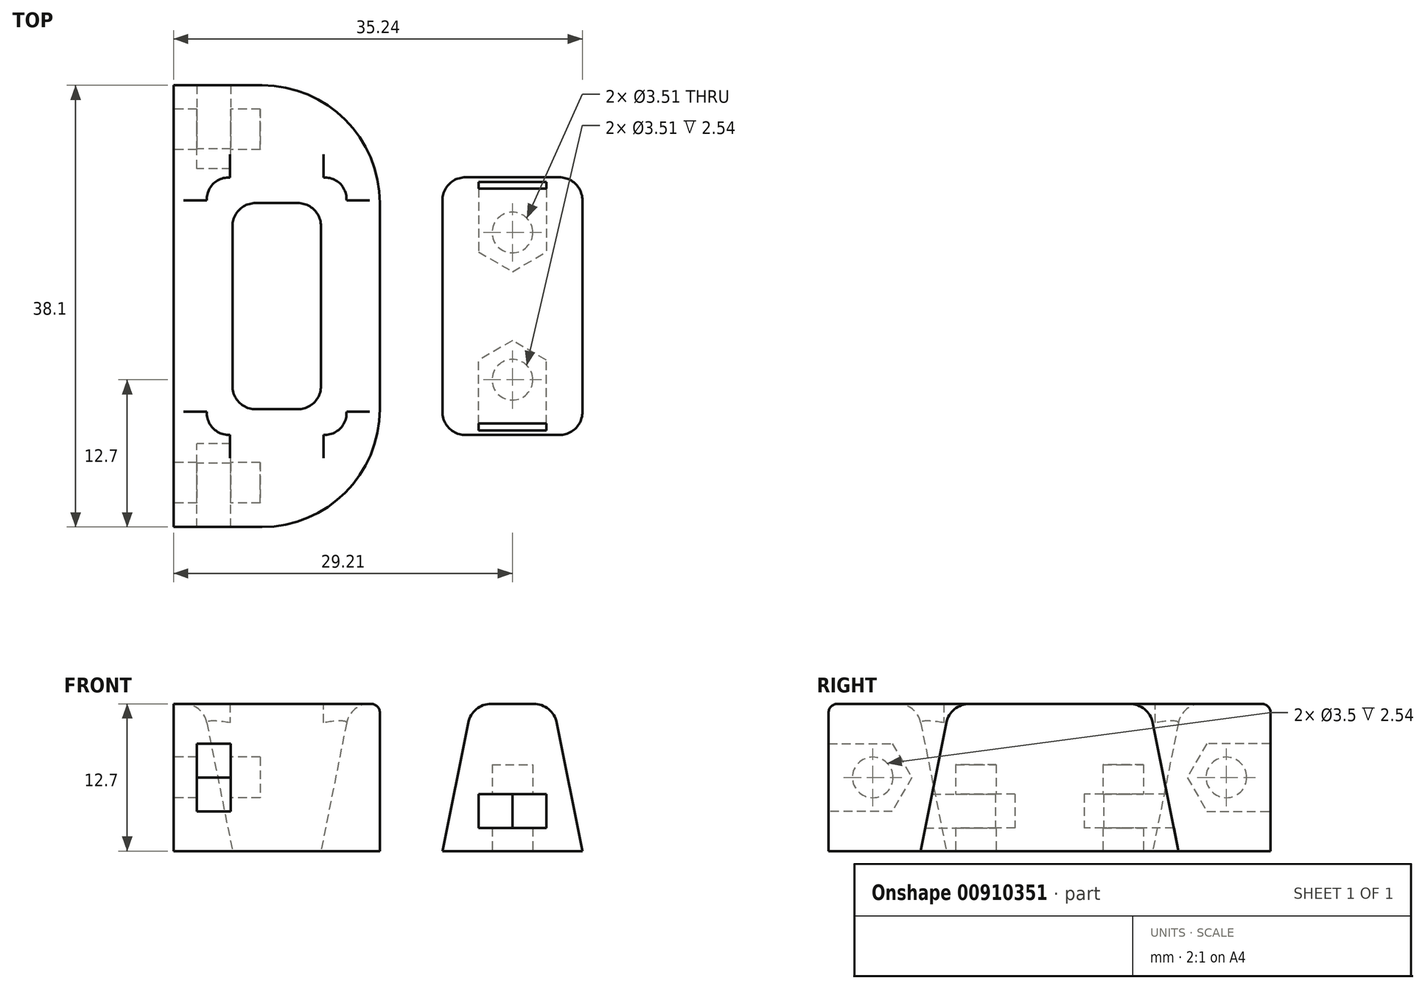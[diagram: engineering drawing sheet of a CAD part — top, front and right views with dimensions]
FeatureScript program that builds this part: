
annotation { "Feature Type Name" : "Feature", "Feature Type Description" : "" }
export const myFeature = defineFeature(function(context is Context, id is Id, definition is map)
    precondition{}
    {
        {
            var Q0;
            Q0=qCreatedBy(makeId("Top.planeOp"),FACE);
            var sketch = newSketch(context, id + "F0", { "sketchPlane" : qUnion([Q0])});
            skLineSegment(sketch, "E0.bottom", {"start": v(3.81, 8.9) * mm, "end": v(-3.81, 8.9) * mm});
            skLineSegment(sketch, "E0.top", {"start": v(3.81, -8.9) * mm, "end": v(-3.81, -8.9) * mm});
            skLineSegment(sketch, "E0.left", {"start": v(3.81, 8.9) * mm, "end": v(3.81, -8.9) * mm});
            skLineSegment(sketch, "E0.right", {"start": v(-3.8, 8.9) * mm, "end": v(-3.81, -8.9) * mm});
            skPoint(sketch, "E0.middle", {"position": v(0, 0) * mm});
            skLineSegment(sketch, "E1.bottom", {"start": v(8.89, 19.05) * mm, "end": v(-8.9, 19.05) * mm});
            skLineSegment(sketch, "E1.top", {"start": v(8.9, -19.05) * mm, "end": v(-8.89, -19.05) * mm});
            skLineSegment(sketch, "E1.left", {"start": v(8.89, 19.05) * mm, "end": v(8.9, -19.05) * mm});
            skLineSegment(sketch, "E1.right", {"start": v(-8.9, 19.05) * mm, "end": v(-8.89, -19.05) * mm});
            skSolve(sketch);
        }
        {
            var Q0;
            Q0 = qSketchRegion(id + "F0", true);
            extrude(context, id + "F1", {"entities" : qUnion([Q0]), "depth" : 12.7 * mm, "offsetDistance" : 25.4 * mm, "symmetric" : true});
        }
        {
            var Q0;
            Q0=makeQuery(id+"F1.opExtrude","CAP_EDGE",EDGE,{"disambiguationData":[OSD([sQuery(id+"F0.wireOp",EDGE,"CVcWmtmA-dy5A-Ui8y-UEql-0ctuhsr9CVpZ")])],"isStart":false});
            var Q1;
            Q1=makeQuery(id+"F1.opExtrude","CAP_EDGE",EDGE,{"disambiguationData":[OSD([sQuery(id+"F0.wireOp",EDGE,"E0.left")])],"isStart":false});
            var Q2;
            Q2=makeQuery(id+"F1.opExtrude","CAP_EDGE",EDGE,{"disambiguationData":[OSD([sQuery(id+"F0.wireOp",EDGE,"E0.bottom")])],"isStart":false});
            var Q3;
            Q3=makeQuery(id+"F1.opExtrude","CAP_EDGE",EDGE,{"disambiguationData":[OSD([sQuery(id+"F0.wireOp",EDGE,"E0.right")])],"isStart":false});
            var Q4;
            Q4=makeQuery(id+"F1.opExtrude","CAP_EDGE",EDGE,{"disambiguationData":[OSD([sQuery(id+"F0.wireOp",EDGE,"E0.top")])],"isStart":false});
            chamfer(context, id + "F2", {"entities" : qUnion([Q0, Q1, Q2, Q3, Q4]), "chamferType" : ChamferType.TWO_OFFSETS, "width1" : 2.54 * mm, "oppositeDirection" : false, "width2" : 12.7 * mm, "tangentPropagation" : true});
        }
        {
            var Q0;
            Q0=makeQuery(id+"F1.opExtrude","SWEPT_FACE",FACE,{"disambiguationData":[OSD([sQuery(id+"F0.wireOp",EDGE,"E1.right")])]});
            var sketch = newSketch(context, id + "F3", { "sketchPlane" : qUnion([Q0])});
            skCircle(sketch, "E2", {"center": v(15.24, 0) * mm, "radius": 1.75 * mm});
            skCircle(sketch, "E3", {"center": v(-15.24, 0) * mm, "radius": 1.75 * mm});
            skLineSegment(sketch, "E4", {"start": v(-15.24, 0) * mm, "end": v(15.24, 0) * mm, "construction": true});
            skSolve(sketch);
        }
        {
            var Q0;
            Q0 = qSketchRegion(id + "F3", true);
            extrude(context, id + "F4", {"entities" : qUnion([Q0]), "operationType" : NewBodyOperationType.REMOVE, "oppositeDirection" : true, "depth" : 2 * mm, "offsetDistance" : 25.4 * mm});
        }
        {
            var Q0;
            Q0=makeQuery(id+"F4.boolean.opBoolean","COPY",FACE,{"derivedFrom":makeQuery(id+"F4.opExtrude","CAP_FACE",FACE,{"disambiguationData":[OSD([sQuery(id+"F3.wireOp",EDGE,"E3")])],"isStart":false})});
            var sketch = newSketch(context, id + "F5", { "sketchPlane" : qUnion([Q0])});
            skLineSegment(sketch, "E5", {"start": v(-19.05, 2.92) * mm, "end": v(-13.55, 2.92) * mm});
            skLineSegment(sketch, "E6", {"start": v(-13.55, 2.92) * mm, "end": v(-11.87, 0) * mm});
            skLineSegment(sketch, "E7", {"start": v(-11.87, 0) * mm, "end": v(-13.55, -2.92) * mm});
            skLineSegment(sketch, "E8", {"start": v(-13.55, -2.92) * mm, "end": v(-19.05, -2.92) * mm});
            skLineSegment(sketch, "E9", {"start": v(-19.05, -2.92) * mm, "end": v(-19.05, 2.92) * mm});
            skLineSegment(sketch, "E10", {"start": v(19.05, 2.92) * mm, "end": v(13.55, 2.92) * mm});
            skLineSegment(sketch, "E11", {"start": v(13.55, 2.92) * mm, "end": v(11.87, 0) * mm});
            skLineSegment(sketch, "E12", {"start": v(11.87, 0) * mm, "end": v(13.55, -2.92) * mm});
            skLineSegment(sketch, "E13", {"start": v(13.55, -2.92) * mm, "end": v(19.05, -2.92) * mm});
            skLineSegment(sketch, "E14", {"start": v(19.05, -2.92) * mm, "end": v(19.05, 2.92) * mm});
            skLineSegment(sketch, "E15", {"start": v(-13.55, 2.92) * mm, "end": v(-15.24, 0) * mm, "construction": true});
            skLineSegment(sketch, "E16", {"start": v(-15.24, 0) * mm, "end": v(-11.87, 0) * mm, "construction": true});
            skLineSegment(sketch, "E17", {"start": v(13.55, 2.92) * mm, "end": v(15.24, 0) * mm, "construction": true});
            skLineSegment(sketch, "E18", {"start": v(15.24, 0) * mm, "end": v(11.87, 0) * mm, "construction": true});
            skSolve(sketch);
        }
        {
            var Q0;
            Q0 = qSketchRegion(id + "F5", true);
            extrude(context, id + "F6", {"entities" : qUnion([Q0]), "operationType" : NewBodyOperationType.REMOVE, "oppositeDirection" : true, "depth" : 2.92 * mm, "offsetDistance" : 25.4 * mm});
        }
        {
            var Q0;
            Q0=makeQuery(id+"F6.boolean.opBoolean","COPY",FACE,{"derivedFrom":makeQuery(id+"F6.opExtrude","CAP_FACE",FACE,{"disambiguationData":[OSD([sQuery(id+"F5.wireOp",EDGE,"E5"),sQuery(id+"F5.wireOp",EDGE,"E6"),sQuery(id+"F5.wireOp",EDGE,"E7"),sQuery(id+"F5.wireOp",EDGE,"E8"),sQuery(id+"F5.wireOp",EDGE,"E9")])],"isStart":false})});
            var sketch = newSketch(context, id + "F7", { "sketchPlane" : qUnion([Q0])});
            skCircle(sketch, "E19.0", {"center": v(-15.24, 0) * mm, "radius": 1.75 * mm});
            skCircle(sketch, "E19.1", {"center": v(15.24, 0) * mm, "radius": 1.75 * mm});
            skSolve(sketch);
        }
        {
            var Q0;
            Q0 = qSketchRegion(id + "F7", true);
            extrude(context, id + "F8", {"entities" : qUnion([Q0]), "operationType" : NewBodyOperationType.REMOVE, "oppositeDirection" : true, "depth" : 2.54 * mm, "offsetDistance" : 25.4 * mm});
        }
        {
            var Q0;
            Q0=qCreatedBy(makeId("Top.planeOp"),FACE);
            var sketch = newSketch(context, id + "F9", { "sketchPlane" : qUnion([Q0])});
            skLineSegment(sketch, "E20", {"start": v(0, 0) * mm, "end": v(20.32, 0) * mm, "construction": true});
            skLineSegment(sketch, "E21.bottom", {"start": v(26.35, -11.11) * mm, "end": v(14.29, -11.11) * mm});
            skLineSegment(sketch, "E21.top", {"start": v(26.35, 11.11) * mm, "end": v(14.29, 11.11) * mm});
            skLineSegment(sketch, "E21.left", {"start": v(26.35, -11.11) * mm, "end": v(26.35, 11.11) * mm});
            skLineSegment(sketch, "E21.right", {"start": v(14.29, -11.11) * mm, "end": v(14.29, 11.11) * mm});
            skPoint(sketch, "E21.middle", {"position": v(20.32, 0) * mm});
            skSolve(sketch);
        }
        {
            var Q0;
            Q0 = qSketchRegion(id + "F9", true);
            extrude(context, id + "F10", {"entities" : qUnion([Q0]), "depth" : 12.7 * mm, "offsetDistance" : 25.4 * mm, "symmetric" : true});
        }
        {
            var Q0;
            Q0=makeQuery(id+"F10.opExtrude","CAP_EDGE",EDGE,{"disambiguationData":[OSD([sQuery(id+"F9.wireOp",EDGE,"E21.right")])],"isStart":false});
            var Q1;
            Q1=makeQuery(id+"F10.opExtrude","CAP_EDGE",EDGE,{"disambiguationData":[OSD([sQuery(id+"F9.wireOp",EDGE,"E21.bottom")])],"isStart":false});
            var Q2;
            Q2=makeQuery(id+"F10.opExtrude","CAP_EDGE",EDGE,{"disambiguationData":[OSD([sQuery(id+"F9.wireOp",EDGE,"E21.left")])],"isStart":false});
            var Q3;
            Q3=makeQuery(id+"F10.opExtrude","CAP_EDGE",EDGE,{"disambiguationData":[OSD([sQuery(id+"F9.wireOp",EDGE,"E21.top")])],"isStart":false});
            chamfer(context, id + "F11", {"entities" : qUnion([Q0, Q1, Q2, Q3]), "chamferType" : ChamferType.TWO_OFFSETS, "width1" : 12.7 * mm, "oppositeDirection" : false, "width2" : 2.54 * mm, "tangentPropagation" : true});
        }
        {
            var Q0;
            Q0=makeQuery(id+"F10.opExtrude","CAP_FACE",FACE,{"disambiguationData":[OSD([sQuery(id+"F9.wireOp",EDGE,"E21.bottom"),sQuery(id+"F9.wireOp",EDGE,"E21.top"),sQuery(id+"F9.wireOp",EDGE,"E21.left"),sQuery(id+"F9.wireOp",EDGE,"E21.right")])],"isStart":true});
            var sketch = newSketch(context, id + "F12", { "sketchPlane" : qUnion([Q0])});
            skCircle(sketch, "E22", {"center": v(20.32, 6.35) * mm, "radius": 1.75 * mm});
            skCircle(sketch, "E23", {"center": v(20.32, -6.35) * mm, "radius": 1.75 * mm});
            skLineSegment(sketch, "E24", {"start": v(20.32, 6.35) * mm, "end": v(20.32, -6.35) * mm});
            skLineSegment(sketch, "E25", {"start": v(26.35, 11.11) * mm, "end": v(20.32, 0) * mm, "construction": true});
            skLineSegment(sketch, "E26", {"start": v(20.32, 0) * mm, "end": v(14.29, -11.11) * mm, "construction": true});
            skSolve(sketch);
        }
        {
            var Q0;
            Q0 = qSketchRegion(id + "F12", true);
            extrude(context, id + "F13", {"entities" : qUnion([Q0]), "operationType" : NewBodyOperationType.REMOVE, "oppositeDirection" : true, "depth" : 2 * mm, "offsetDistance" : 25.4 * mm});
        }
        {
            var Q0;
            Q0=makeQuery(id+"F13.boolean.opBoolean","COPY",FACE,{"derivedFrom":makeQuery(id+"F13.opExtrude","CAP_FACE",FACE,{"disambiguationData":[OSD([sQuery(id+"F12.wireOp",EDGE,"E22")])],"isStart":false})});
            var sketch = newSketch(context, id + "F14", { "sketchPlane" : qUnion([Q0])});
            skCircle(sketch, "E27.cCircle", {"center": v(20.32, 6.35) * mm, "radius": 2.92 * mm, "construction": true});
            skLineSegment(sketch, "E27.0", {"start": v(23.24, 8.04) * mm, "end": v(23.24, 4.66) * mm});
            skLineSegment(sketch, "E27.1", {"start": v(23.24, 4.66) * mm, "end": v(20.32, 2.98) * mm});
            skLineSegment(sketch, "E27.2", {"start": v(20.32, 2.98) * mm, "end": v(17.4, 4.66) * mm});
            skLineSegment(sketch, "E27.3", {"start": v(17.4, 4.66) * mm, "end": v(17.4, 8.04) * mm});
            skLineSegment(sketch, "E27.4", {"start": v(17.4, 8.04) * mm, "end": v(20.32, 9.72) * mm, "construction": true});
            skLineSegment(sketch, "E27.5", {"start": v(20.32, 9.72) * mm, "end": v(23.24, 8.04) * mm, "construction": true});
            skPoint(sketch, "E27.0.midPoint", {"position": v(23.24, 6.35) * mm});
            skCircle(sketch, "E28.cCircle", {"center": v(20.32, -6.35) * mm, "radius": 2.92 * mm, "construction": true});
            skLineSegment(sketch, "E28.0", {"start": v(23.24, -4.66) * mm, "end": v(23.24, -8.04) * mm});
            skLineSegment(sketch, "E28.1", {"start": v(23.24, -8.04) * mm, "end": v(20.32, -9.72) * mm, "construction": true});
            skLineSegment(sketch, "E28.2", {"start": v(20.32, -9.72) * mm, "end": v(17.4, -8.04) * mm, "construction": true});
            skLineSegment(sketch, "E28.3", {"start": v(17.4, -8.04) * mm, "end": v(17.4, -4.66) * mm});
            skLineSegment(sketch, "E28.4", {"start": v(17.4, -4.66) * mm, "end": v(20.32, -2.98) * mm});
            skLineSegment(sketch, "E28.5", {"start": v(20.32, -2.98) * mm, "end": v(23.24, -4.66) * mm});
            skPoint(sketch, "E28.0.midPoint", {"position": v(23.24, -6.35) * mm});
            skLineSegment(sketch, "E29", {"start": v(23.24, 8.04) * mm, "end": v(23.24, 11.11) * mm});
            skLineSegment(sketch, "E30", {"start": v(23.24, 11.11) * mm, "end": v(17.4, 11.11) * mm});
            skLineSegment(sketch, "E31", {"start": v(17.4, 11.11) * mm, "end": v(17.4, 8.04) * mm});
            skLineSegment(sketch, "E32", {"start": v(17.4, -8.04) * mm, "end": v(17.4, -11.11) * mm});
            skLineSegment(sketch, "E33", {"start": v(17.4, -11.11) * mm, "end": v(23.24, -11.11) * mm});
            skLineSegment(sketch, "E34", {"start": v(23.24, -11.11) * mm, "end": v(23.24, -8.04) * mm});
            skSolve(sketch);
        }
        {
            var Q0;
            Q0 = qSketchRegion(id + "F14", true);
            extrude(context, id + "F15", {"entities" : qUnion([Q0]), "operationType" : NewBodyOperationType.REMOVE, "oppositeDirection" : true, "depth" : 2.92 * mm, "offsetDistance" : 25.4 * mm});
        }
        {
            var Q0;
            Q0=makeQuery(id+"F15.boolean.opBoolean","COPY",FACE,{"derivedFrom":makeQuery(id+"F15.opExtrude","CAP_FACE",FACE,{"disambiguationData":[OSD([sQuery(id+"F14.wireOp",EDGE,"E27.0"),sQuery(id+"F14.wireOp",EDGE,"E27.1"),sQuery(id+"F14.wireOp",EDGE,"E27.2"),sQuery(id+"F14.wireOp",EDGE,"E27.3"),sQuery(id+"F14.wireOp",EDGE,"E29"),sQuery(id+"F14.wireOp",EDGE,"E30"),sQuery(id+"F14.wireOp",EDGE,"E31")])],"isStart":false})});
            var sketch = newSketch(context, id + "F16", { "sketchPlane" : qUnion([Q0])});
            skCircle(sketch, "E35.0", {"center": v(20.32, 6.35) * mm, "radius": 1.75 * mm});
            skCircle(sketch, "E35.1", {"center": v(20.32, -6.35) * mm, "radius": 1.75 * mm});
            skSolve(sketch);
        }
        {
            var Q0;
            Q0 = qSketchRegion(id + "F16", true);
            extrude(context, id + "F17", {"entities" : qUnion([Q0]), "operationType" : NewBodyOperationType.REMOVE, "oppositeDirection" : true, "depth" : 2.54 * mm, "offsetDistance" : 25.4 * mm});
        }
        {
            var Q0;
            Q0=makeQuery(id+"F1.opExtrude","SWEPT_EDGE",EDGE,{"disambiguationData":[OSD([sQuery(id+"F0.wireOp",EDGE,"E1.top"),sQuery(id+"F0.wireOp",EDGE,"E1.left")])]});
            var Q1;
            Q1=makeQuery(id+"F1.opExtrude","SWEPT_EDGE",EDGE,{"disambiguationData":[OSD([sQuery(id+"F0.wireOp",EDGE,"E1.bottom"),sQuery(id+"F0.wireOp",EDGE,"E1.left")])]});
            fillet(context, id + "F18", {"entities" : qUnion([Q0, Q1]), "radius" : 10.16 * mm, "tangentPropagation" : true, "allowEdgeOverflow" : false});
        }
        {
            var Q0;
            Q0=makeQuery(id+"F11.opChamfer","BLEND_EDGE",EDGE,{"blendedFrom":[makeQuery(id+"F10.opExtrude","CAP_EDGE",EDGE,{"disambiguationData":[OSD([sQuery(id+"F9.wireOp",EDGE,"E21.top")])],"isStart":false}),makeQuery(id+"F10.opExtrude","CAP_EDGE",EDGE,{"disambiguationData":[OSD([sQuery(id+"F9.wireOp",EDGE,"E21.right")])],"isStart":false})],"blendedInto":[]});
            var Q1;
            Q1=makeQuery(id+"F11.opChamfer","BLEND_EDGE",EDGE,{"blendedFrom":[makeQuery(id+"F10.opExtrude","CAP_EDGE",EDGE,{"disambiguationData":[OSD([sQuery(id+"F9.wireOp",EDGE,"E21.bottom")])],"isStart":false}),makeQuery(id+"F10.opExtrude","CAP_EDGE",EDGE,{"disambiguationData":[OSD([sQuery(id+"F9.wireOp",EDGE,"E21.right")])],"isStart":false})],"blendedInto":[]});
            var Q2;
            Q2=makeQuery(id+"F11.opChamfer","BLEND_EDGE",EDGE,{"blendedFrom":[makeQuery(id+"F10.opExtrude","CAP_EDGE",EDGE,{"disambiguationData":[OSD([sQuery(id+"F9.wireOp",EDGE,"E21.bottom")])],"isStart":false}),makeQuery(id+"F10.opExtrude","CAP_EDGE",EDGE,{"disambiguationData":[OSD([sQuery(id+"F9.wireOp",EDGE,"E21.left")])],"isStart":false})],"blendedInto":[]});
            var Q3;
            Q3=makeQuery(id+"F11.opChamfer","BLEND_EDGE",EDGE,{"blendedFrom":[makeQuery(id+"F10.opExtrude","CAP_EDGE",EDGE,{"disambiguationData":[OSD([sQuery(id+"F9.wireOp",EDGE,"E21.top")])],"isStart":false}),makeQuery(id+"F10.opExtrude","CAP_EDGE",EDGE,{"disambiguationData":[OSD([sQuery(id+"F9.wireOp",EDGE,"E21.left")])],"isStart":false})],"blendedInto":[]});
            var Q4;
            {var subQ0=sQuery(id+"F9.wireOp",EDGE,"E21.right");Q4=makeQuery(id+"F11.opChamfer","BLEND_EDGE",EDGE,{"blendedFrom":[makeQuery(id+"F10.opExtrude","CAP_EDGE",EDGE,{"disambiguationData":[OSD([subQ0])],"isStart":false}),makeQuery(id+"F10.opExtrude","CAP_FACE",FACE,{"disambiguationData":[OSD([sQuery(id+"F9.wireOp",EDGE,"E21.bottom"),sQuery(id+"F9.wireOp",EDGE,"E21.top"),sQuery(id+"F9.wireOp",EDGE,"E21.left"),subQ0])],"isStart":false})],"blendedInto":[makeQuery(id+"F10.opExtrude","CAP_FACE",FACE,{"disambiguationData":[OSD([sQuery(id+"F9.wireOp",EDGE,"E21.bottom"),sQuery(id+"F9.wireOp",EDGE,"E21.top"),sQuery(id+"F9.wireOp",EDGE,"E21.left"),subQ0])],"isStart":false})]});}
            var Q5;
            {var subQ0=sQuery(id+"F9.wireOp",EDGE,"E21.bottom");Q5=makeQuery(id+"F11.opChamfer","BLEND_EDGE",EDGE,{"blendedFrom":[makeQuery(id+"F10.opExtrude","CAP_EDGE",EDGE,{"disambiguationData":[OSD([subQ0])],"isStart":false}),makeQuery(id+"F10.opExtrude","CAP_FACE",FACE,{"disambiguationData":[OSD([subQ0,sQuery(id+"F9.wireOp",EDGE,"E21.top"),sQuery(id+"F9.wireOp",EDGE,"E21.left"),sQuery(id+"F9.wireOp",EDGE,"E21.right")])],"isStart":false})],"blendedInto":[makeQuery(id+"F10.opExtrude","CAP_FACE",FACE,{"disambiguationData":[OSD([subQ0,sQuery(id+"F9.wireOp",EDGE,"E21.top"),sQuery(id+"F9.wireOp",EDGE,"E21.left"),sQuery(id+"F9.wireOp",EDGE,"E21.right")])],"isStart":false})]});}
            var Q6;
            {var subQ0=sQuery(id+"F9.wireOp",EDGE,"E21.left");Q6=makeQuery(id+"F11.opChamfer","BLEND_EDGE",EDGE,{"blendedFrom":[makeQuery(id+"F10.opExtrude","CAP_EDGE",EDGE,{"disambiguationData":[OSD([subQ0])],"isStart":false}),makeQuery(id+"F10.opExtrude","CAP_FACE",FACE,{"disambiguationData":[OSD([sQuery(id+"F9.wireOp",EDGE,"E21.bottom"),sQuery(id+"F9.wireOp",EDGE,"E21.top"),subQ0,sQuery(id+"F9.wireOp",EDGE,"E21.right")])],"isStart":false})],"blendedInto":[makeQuery(id+"F10.opExtrude","CAP_FACE",FACE,{"disambiguationData":[OSD([sQuery(id+"F9.wireOp",EDGE,"E21.bottom"),sQuery(id+"F9.wireOp",EDGE,"E21.top"),subQ0,sQuery(id+"F9.wireOp",EDGE,"E21.right")])],"isStart":false})]});}
            var Q7;
            {var subQ0=sQuery(id+"F9.wireOp",EDGE,"E21.top");Q7=makeQuery(id+"F11.opChamfer","BLEND_EDGE",EDGE,{"blendedFrom":[makeQuery(id+"F10.opExtrude","CAP_EDGE",EDGE,{"disambiguationData":[OSD([subQ0])],"isStart":false}),makeQuery(id+"F10.opExtrude","CAP_FACE",FACE,{"disambiguationData":[OSD([sQuery(id+"F9.wireOp",EDGE,"E21.bottom"),subQ0,sQuery(id+"F9.wireOp",EDGE,"E21.left"),sQuery(id+"F9.wireOp",EDGE,"E21.right")])],"isStart":false})],"blendedInto":[makeQuery(id+"F10.opExtrude","CAP_FACE",FACE,{"disambiguationData":[OSD([sQuery(id+"F9.wireOp",EDGE,"E21.bottom"),subQ0,sQuery(id+"F9.wireOp",EDGE,"E21.left"),sQuery(id+"F9.wireOp",EDGE,"E21.right")])],"isStart":false})]});}
            fillet(context, id + "F19", {"entities" : qUnion([Q0, Q1, Q2, Q3, Q4, Q5, Q6, Q7]), "radius" : 2.03 * mm, "tangentPropagation" : true, "allowEdgeOverflow" : false});
        }
        {
            var Q0;
            Q0=makeQuery(id+"F2.opChamfer","BLEND_EDGE",EDGE,{"blendedFrom":[makeQuery(id+"F1.opExtrude","CAP_EDGE",EDGE,{"disambiguationData":[OSD([sQuery(id+"F0.wireOp",EDGE,"E0.bottom")])],"isStart":false}),makeQuery(id+"F1.opExtrude","CAP_EDGE",EDGE,{"disambiguationData":[OSD([sQuery(id+"F0.wireOp",EDGE,"E0.left")])],"isStart":false})],"blendedInto":[]});
            var Q1;
            Q1=makeQuery(id+"F2.opChamfer","BLEND_EDGE",EDGE,{"blendedFrom":[makeQuery(id+"F1.opExtrude","CAP_EDGE",EDGE,{"disambiguationData":[OSD([sQuery(id+"F0.wireOp",EDGE,"E0.top")])],"isStart":false}),makeQuery(id+"F1.opExtrude","CAP_EDGE",EDGE,{"disambiguationData":[OSD([sQuery(id+"F0.wireOp",EDGE,"E0.left")])],"isStart":false})],"blendedInto":[]});
            var Q2;
            Q2=makeQuery(id+"F2.opChamfer","BLEND_EDGE",EDGE,{"blendedFrom":[makeQuery(id+"F1.opExtrude","CAP_EDGE",EDGE,{"disambiguationData":[OSD([sQuery(id+"F0.wireOp",EDGE,"E0.top")])],"isStart":false}),makeQuery(id+"F1.opExtrude","CAP_EDGE",EDGE,{"disambiguationData":[OSD([sQuery(id+"F0.wireOp",EDGE,"E0.right")])],"isStart":false})],"blendedInto":[]});
            var Q3;
            Q3=makeQuery(id+"F2.opChamfer","BLEND_EDGE",EDGE,{"blendedFrom":[makeQuery(id+"F1.opExtrude","CAP_EDGE",EDGE,{"disambiguationData":[OSD([sQuery(id+"F0.wireOp",EDGE,"E0.bottom")])],"isStart":false}),makeQuery(id+"F1.opExtrude","CAP_EDGE",EDGE,{"disambiguationData":[OSD([sQuery(id+"F0.wireOp",EDGE,"E0.right")])],"isStart":false})],"blendedInto":[]});
            var Q4;
            {var subQ0=sQuery(id+"F0.wireOp",EDGE,"E0.bottom");Q4=makeQuery(id+"F2.opChamfer","BLEND_EDGE",EDGE,{"blendedFrom":[makeQuery(id+"F1.opExtrude","CAP_EDGE",EDGE,{"disambiguationData":[OSD([subQ0])],"isStart":false}),makeQuery(id+"F1.opExtrude","CAP_FACE",FACE,{"disambiguationData":[OSD([subQ0,sQuery(id+"F0.wireOp",EDGE,"E0.top"),sQuery(id+"F0.wireOp",EDGE,"E0.left"),sQuery(id+"F0.wireOp",EDGE,"E0.right"),sQuery(id+"F0.wireOp",EDGE,"E1.bottom"),sQuery(id+"F0.wireOp",EDGE,"E1.top"),sQuery(id+"F0.wireOp",EDGE,"E1.left"),sQuery(id+"F0.wireOp",EDGE,"E1.right")])],"isStart":false})],"blendedInto":[makeQuery(id+"F1.opExtrude","CAP_FACE",FACE,{"disambiguationData":[OSD([subQ0,sQuery(id+"F0.wireOp",EDGE,"E0.top"),sQuery(id+"F0.wireOp",EDGE,"E0.left"),sQuery(id+"F0.wireOp",EDGE,"E0.right"),sQuery(id+"F0.wireOp",EDGE,"E1.bottom"),sQuery(id+"F0.wireOp",EDGE,"E1.top"),sQuery(id+"F0.wireOp",EDGE,"E1.left"),sQuery(id+"F0.wireOp",EDGE,"E1.right")])],"isStart":false})]});}
            var Q5;
            {var subQ0=sQuery(id+"F0.wireOp",EDGE,"E0.left");Q5=makeQuery(id+"F2.opChamfer","BLEND_EDGE",EDGE,{"blendedFrom":[makeQuery(id+"F1.opExtrude","CAP_EDGE",EDGE,{"disambiguationData":[OSD([subQ0])],"isStart":false}),makeQuery(id+"F1.opExtrude","CAP_FACE",FACE,{"disambiguationData":[OSD([sQuery(id+"F0.wireOp",EDGE,"E0.bottom"),sQuery(id+"F0.wireOp",EDGE,"E0.top"),subQ0,sQuery(id+"F0.wireOp",EDGE,"E0.right"),sQuery(id+"F0.wireOp",EDGE,"E1.bottom"),sQuery(id+"F0.wireOp",EDGE,"E1.top"),sQuery(id+"F0.wireOp",EDGE,"E1.left"),sQuery(id+"F0.wireOp",EDGE,"E1.right")])],"isStart":false})],"blendedInto":[makeQuery(id+"F1.opExtrude","CAP_FACE",FACE,{"disambiguationData":[OSD([sQuery(id+"F0.wireOp",EDGE,"E0.bottom"),sQuery(id+"F0.wireOp",EDGE,"E0.top"),subQ0,sQuery(id+"F0.wireOp",EDGE,"E0.right"),sQuery(id+"F0.wireOp",EDGE,"E1.bottom"),sQuery(id+"F0.wireOp",EDGE,"E1.top"),sQuery(id+"F0.wireOp",EDGE,"E1.left"),sQuery(id+"F0.wireOp",EDGE,"E1.right")])],"isStart":false})]});}
            var Q6;
            {var subQ0=sQuery(id+"F0.wireOp",EDGE,"E0.top");Q6=makeQuery(id+"F2.opChamfer","BLEND_EDGE",EDGE,{"blendedFrom":[makeQuery(id+"F1.opExtrude","CAP_EDGE",EDGE,{"disambiguationData":[OSD([subQ0])],"isStart":false}),makeQuery(id+"F1.opExtrude","CAP_FACE",FACE,{"disambiguationData":[OSD([sQuery(id+"F0.wireOp",EDGE,"E0.bottom"),subQ0,sQuery(id+"F0.wireOp",EDGE,"E0.left"),sQuery(id+"F0.wireOp",EDGE,"E0.right"),sQuery(id+"F0.wireOp",EDGE,"E1.bottom"),sQuery(id+"F0.wireOp",EDGE,"E1.top"),sQuery(id+"F0.wireOp",EDGE,"E1.left"),sQuery(id+"F0.wireOp",EDGE,"E1.right")])],"isStart":false})],"blendedInto":[makeQuery(id+"F1.opExtrude","CAP_FACE",FACE,{"disambiguationData":[OSD([sQuery(id+"F0.wireOp",EDGE,"E0.bottom"),subQ0,sQuery(id+"F0.wireOp",EDGE,"E0.left"),sQuery(id+"F0.wireOp",EDGE,"E0.right"),sQuery(id+"F0.wireOp",EDGE,"E1.bottom"),sQuery(id+"F0.wireOp",EDGE,"E1.top"),sQuery(id+"F0.wireOp",EDGE,"E1.left"),sQuery(id+"F0.wireOp",EDGE,"E1.right")])],"isStart":false})]});}
            var Q7;
            {var subQ0=sQuery(id+"F0.wireOp",EDGE,"E0.right");Q7=makeQuery(id+"F2.opChamfer","BLEND_EDGE",EDGE,{"blendedFrom":[makeQuery(id+"F1.opExtrude","CAP_EDGE",EDGE,{"disambiguationData":[OSD([subQ0])],"isStart":false}),makeQuery(id+"F1.opExtrude","CAP_FACE",FACE,{"disambiguationData":[OSD([sQuery(id+"F0.wireOp",EDGE,"E0.bottom"),sQuery(id+"F0.wireOp",EDGE,"E0.top"),sQuery(id+"F0.wireOp",EDGE,"E0.left"),subQ0,sQuery(id+"F0.wireOp",EDGE,"E1.bottom"),sQuery(id+"F0.wireOp",EDGE,"E1.top"),sQuery(id+"F0.wireOp",EDGE,"E1.left"),sQuery(id+"F0.wireOp",EDGE,"E1.right")])],"isStart":false})],"blendedInto":[makeQuery(id+"F1.opExtrude","CAP_FACE",FACE,{"disambiguationData":[OSD([sQuery(id+"F0.wireOp",EDGE,"E0.bottom"),sQuery(id+"F0.wireOp",EDGE,"E0.top"),sQuery(id+"F0.wireOp",EDGE,"E0.left"),subQ0,sQuery(id+"F0.wireOp",EDGE,"E1.bottom"),sQuery(id+"F0.wireOp",EDGE,"E1.top"),sQuery(id+"F0.wireOp",EDGE,"E1.left"),sQuery(id+"F0.wireOp",EDGE,"E1.right")])],"isStart":false})]});}
            fillet(context, id + "F20", {"entities" : qUnion([Q0, Q1, Q2, Q3, Q4, Q5, Q6, Q7]), "radius" : 2.03 * mm, "tangentPropagation" : true, "allowEdgeOverflow" : false});
        }
        {
            var Q0;
            Q0=makeQuery(id+"F1.opExtrude","CAP_EDGE",EDGE,{"disambiguationData":[OSD([sQuery(id+"F0.wireOp",EDGE,"E1.top")])],"isStart":false});
            fillet(context, id + "F21", {"entities" : qUnion([Q0]), "radius" : 0.76 * mm, "tangentPropagation" : true, "allowEdgeOverflow" : false});
        }
    });
